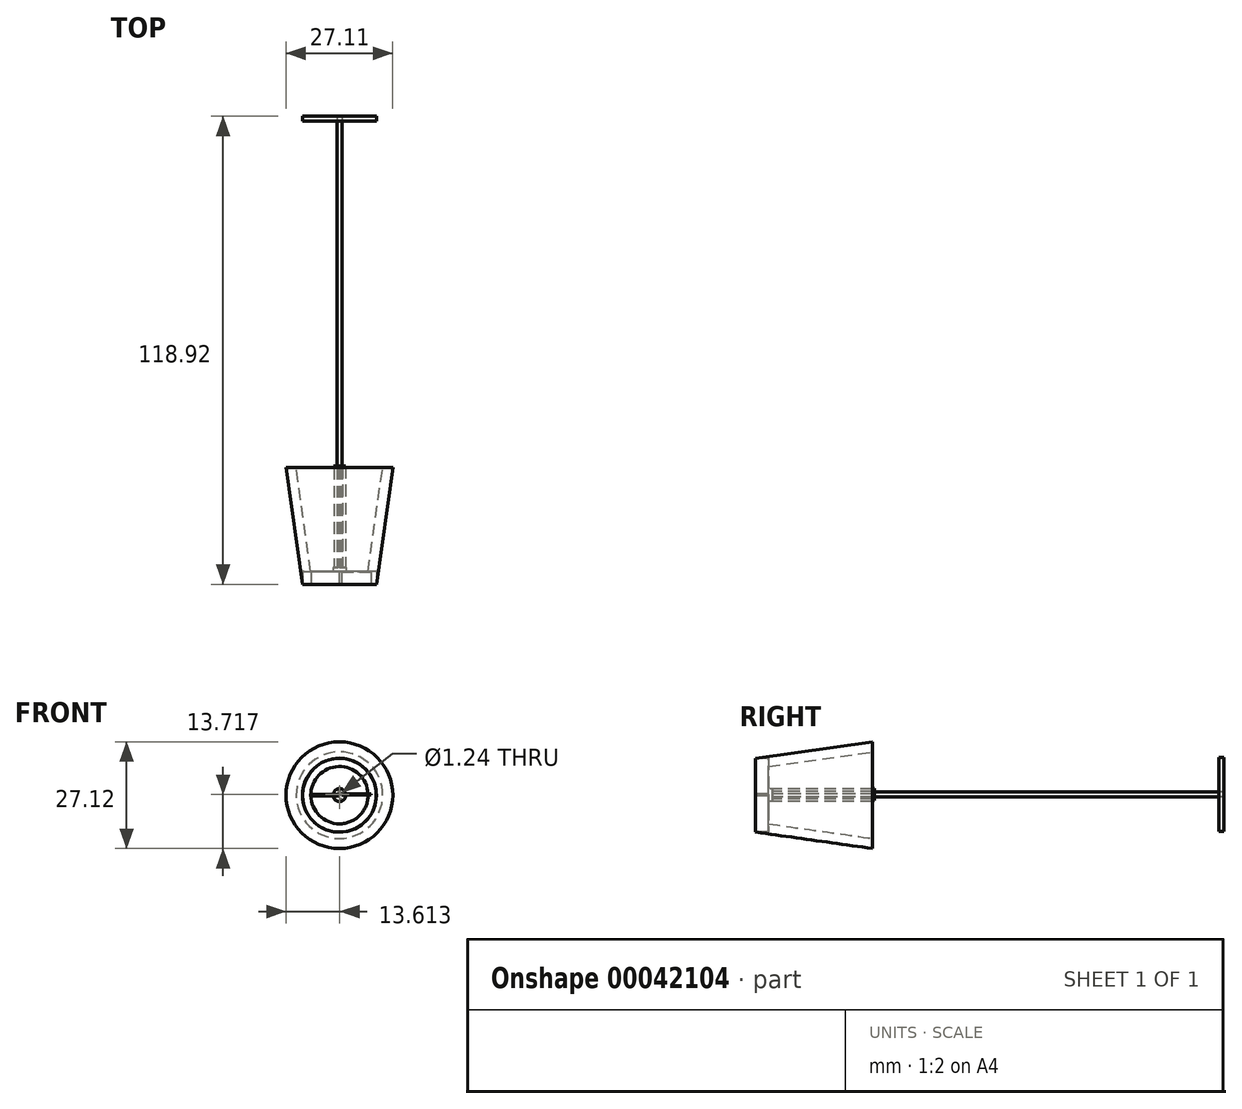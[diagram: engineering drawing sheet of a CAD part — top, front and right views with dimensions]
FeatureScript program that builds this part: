
annotation { "Feature Type Name" : "Feature", "Feature Type Description" : "" }
export const myFeature = defineFeature(function(context is Context, id is Id, definition is map)
    precondition{}
    {
        {
            var Q0;
            Q0=qCreatedBy(makeId("Front.planeOp"),FACE);
            var sketch = newSketch(context, id + "F0", { "sketchPlane" : qUnion([Q0])});
            skCircle(sketch, "E0", {"center": v(-47.5, -26.07) * mm, "radius": 13.56 * mm});
            skSolve(sketch);
        }
        {
            var Q0;
            Q0=makeQuery(id+"F0.imprint","IMPRINT",FACE,{"disambiguationData":[TD([[makeQuery(id+"F0.imprint","IMPRINT",EDGE,{"derivedFrom":sQuery(id+"F0.wireOp",EDGE,"E0")}),1.0]])]});
            extrude(context, id + "F1", {"entities" : qUnion([Q0]), "depth" : 29.72 * mm, "hasDraft" : true, "draftAngle" : 8 * degree, "draftPullDirection" : true});
        }
        {
            var Q0;
            Q0=makeQuery(id+"F1.opExtrude","CAP_FACE",FACE,{"disambiguationData":[OSD([sQuery(id+"F0.wireOp",EDGE,"E0")])],"isStart":true});
            shell(context, id + "F2", {"entities" : qUnion([Q0]), "thickness" : 2.54 * mm});
        }
        {
            var Q0;
            {var subQ0=sQuery(id+"F0.wireOp",EDGE,"E0");Q0=makeQuery(id+"F2.opShell","OFFSET_FACE",FACE,{"disambiguationData":[OSD([subQ0]),TDD([makeQuery(id+"F1.opExtrude","CAP_FACE",FACE,{"disambiguationData":[OSD([subQ0])],"isStart":false})])]});}
            var sketch = newSketch(context, id + "F3", { "sketchPlane" : qUnion([Q0])});
            skCircle(sketch, "E1", {"center": v(47.5, -26.07) * mm, "radius": 1.62 * mm});
            skSolve(sketch);
        }
        {
            var Q0;
            Q0=makeQuery(id+"F3.imprint","IMPRINT",FACE,{"disambiguationData":[TD([[makeQuery(id+"F3.imprint","IMPRINT",EDGE,{"derivedFrom":sQuery(id+"F3.wireOp",EDGE,"E1")}),1.0]])]});
            extrude(context, id + "F4", {"entities" : qUnion([Q0]), "operationType" : NewBodyOperationType.ADD, "depth" : 1.7 * mm});
        }
        {
            var Q0;
            Q0=makeQuery(id+"F4.opExtrude","CAP_FACE",FACE,{"disambiguationData":[OSD([sQuery(id+"F3.wireOp",EDGE,"E1")])],"isStart":false});
            var sketch = newSketch(context, id + "F5", { "sketchPlane" : qUnion([Q0])});
            skCircle(sketch, "E2", {"center": v(46.34, -26.1) * mm, "radius": 0.36 * mm});
            skCircle(sketch, "E3", {"center": v(47.5, -27.23) * mm, "radius": 0.4 * mm});
            skCircle(sketch, "E4", {"center": v(48.59, -26.1) * mm, "radius": 0.38 * mm});
            skCircle(sketch, "E5", {"center": v(47.36, -25.08) * mm, "radius": 0.42 * mm});
            skSolve(sketch);
        }
        {
            var Q0;
            Q0=makeQuery(id+"F5.imprint","IMPRINT",FACE,{"disambiguationData":[TD([[makeQuery(id+"F5.imprint","IMPRINT",EDGE,{"derivedFrom":sQuery(id+"F5.wireOp",EDGE,"E2")}),1.0]])]});
            extrude(context, id + "F6", {"entities" : qUnion([Q0]), "operationType" : NewBodyOperationType.ADD, "depth" : 25.7 * mm});
        }
        {
            var Q0;
            Q0=makeQuery(id+"F4.opExtrude","CAP_FACE",FACE,{"disambiguationData":[OSD([sQuery(id+"F3.wireOp",EDGE,"E1")])],"isStart":false});
            var sketch = newSketch(context, id + "F7", { "sketchPlane" : qUnion([Q0])});
            skCircle(sketch, "E6", {"center": v(48.47, -26.15) * mm, "radius": 0.36 * mm});
            skSolve(sketch);
        }
        {
            var Q0;
            Q0=makeQuery(id+"F7.imprint","IMPRINT",FACE,{"disambiguationData":[TD([[makeQuery(id+"F7.imprint","IMPRINT",EDGE,{"derivedFrom":sQuery(id+"F7.wireOp",EDGE,"E6")}),1.0]])]});
            extrude(context, id + "F8", {"entities" : qUnion([Q0]), "operationType" : NewBodyOperationType.ADD, "depth" : 25.4 * mm});
        }
        {
            var Q0;
            Q0=makeQuery(id+"F4.opExtrude","CAP_FACE",FACE,{"disambiguationData":[OSD([sQuery(id+"F3.wireOp",EDGE,"E1")])],"isStart":false});
            var sketch = newSketch(context, id + "F9", { "sketchPlane" : qUnion([Q0])});
            skCircle(sketch, "E7", {"center": v(47.58, -24.73) * mm, "radius": 0.33 * mm});
            skSolve(sketch);
        }
        {
            var Q0;
            {var subQ0=makeQuery(id+"F4.opExtrude","CAP_EDGE",EDGE,{"disambiguationData":[OSD([sQuery(id+"F3.wireOp",EDGE,"E1")])],"isStart":false});var subQ1=sQuery(id+"F9.wireOp",EDGE,"E7");var subQ3=makeQuery(id+"F9.imprint","INTERSECT",VERTEX,{"disambiguationData":[OD(0.0)],"derivedFrom":[subQ0,subQ1]});Q0=makeQuery(id+"F9.imprint","IMPRINT",FACE,{"disambiguationData":[TD([[makeQuery(id+"F9.imprint","IMPRINT",EDGE,{"disambiguationData":[TD([[subQ3,1.0]])],"derivedFrom":subQ1}),1.0]])]});}
            extrude(context, id + "F10", {"entities" : qUnion([Q0]), "operationType" : NewBodyOperationType.ADD, "depth" : 25.4 * mm});
        }
        {
            var Q0;
            Q0=makeQuery(id+"F4.opExtrude","CAP_FACE",FACE,{"disambiguationData":[OSD([sQuery(id+"F3.wireOp",EDGE,"E1")])],"isStart":false});
            var sketch = newSketch(context, id + "F11", { "sketchPlane" : qUnion([Q0])});
            skCircle(sketch, "E8", {"center": v(47.13, -27.35) * mm, "radius": 0.3 * mm});
            skSolve(sketch);
        }
        {
            var Q0;
            {var subQ0=makeQuery(id+"F4.opExtrude","CAP_EDGE",EDGE,{"disambiguationData":[OSD([sQuery(id+"F3.wireOp",EDGE,"E1")])],"isStart":false});var subQ1=sQuery(id+"F11.wireOp",EDGE,"E8");var subQ3=makeQuery(id+"F11.imprint","INTERSECT",VERTEX,{"disambiguationData":[OD(0.0)],"derivedFrom":[subQ0,subQ1]});Q0=makeQuery(id+"F11.imprint","IMPRINT",FACE,{"disambiguationData":[TD([[makeQuery(id+"F11.imprint","IMPRINT",EDGE,{"disambiguationData":[TD([[subQ3,-1.0]])],"derivedFrom":subQ1}),1.0]])]});}
            extrude(context, id + "F12", {"entities" : qUnion([Q0]), "operationType" : NewBodyOperationType.ADD, "depth" : 25.4 * mm});
        }
        {
            var Q0;
            Q0=makeQuery(id+"F10.opExtrude","CAP_FACE",FACE,{"disambiguationData":[OSD([sQuery(id+"F3.wireOp",EDGE,"E1"),sQuery(id+"F9.wireOp",EDGE,"E7")])],"isStart":false});
            var sketch = newSketch(context, id + "F13", { "sketchPlane" : qUnion([Q0])});
            skCircle(sketch, "E9", {"center": v(47.66, -25.95) * mm, "radius": 1.52 * mm});
            skPoint(sketch, "E9.first.point", {"position": v(47.42, -24.45) * mm});
            skPoint(sketch, "E9.second.point", {"position": v(47.07, -27.35) * mm});
            skPoint(sketch, "E9.third.point", {"position": v(47.42, -27.45) * mm});
            skSolve(sketch);
        }
        {
            var Q0;
            Q0=makeQuery(id+"F13.imprint","IMPRINT",FACE,{"disambiguationData":[TD([[makeQuery(id+"F13.imprint","IMPRINT",EDGE,{"derivedFrom":sQuery(id+"F13.wireOp",EDGE,"E9")}),1.0]])]});
            var sketch = newSketch(context, id + "F14", { "sketchPlane" : qUnion([Q0])});
            skCircle(sketch, "E10", {"center": v(47.44, -25.91) * mm, "radius": 1.54 * mm});
            skSolve(sketch);
        }
        {
            var Q0;
            Q0 = qSketchRegion(id + "F14", true);
            extrude(context, id + "F15", {"entities" : qUnion([Q0]), "depth" : 0.5 * mm});
        }
        {
            var Q0;
            Q0=makeQuery(id+"F15.opExtrude","CAP_FACE",FACE,{"disambiguationData":[OSD([sQuery(id+"F14.wireOp",EDGE,"E10")])],"isStart":false});
            var sketch = newSketch(context, id + "F16", { "sketchPlane" : qUnion([Q0])});
            skCircle(sketch, "E11", {"center": v(47.44, -25.91) * mm, "radius": 0.62 * mm});
            skSolve(sketch);
        }
        {
            var Q0;
            Q0=makeQuery(id+"F16.imprint","IMPRINT",FACE,{"disambiguationData":[TD([[makeQuery(id+"F16.imprint","IMPRINT",EDGE,{"derivedFrom":sQuery(id+"F16.wireOp",EDGE,"E11")}),1.0]])]});
            extrude(context, id + "F17", {"entities" : qUnion([Q0]), "operationType" : NewBodyOperationType.ADD, "depth" : 87.55 * mm});
        }
        {
            var Q0;
            Q0=makeQuery(id+"F17.opExtrude","CAP_FACE",FACE,{"disambiguationData":[OSD([sQuery(id+"F16.wireOp",EDGE,"E11")])],"isStart":false});
            var sketch = newSketch(context, id + "F18", { "sketchPlane" : qUnion([Q0])});
            skCircle(sketch, "E12", {"center": v(47.44, -25.91) * mm, "radius": 9.4 * mm});
            skSolve(sketch);
        }
        {
            var Q0;
            Q0=makeQuery(id+"F18.imprint","IMPRINT",FACE,{"disambiguationData":[TD([[makeQuery(id+"F18.imprint","IMPRINT",EDGE,{"derivedFrom":sQuery(id+"F18.wireOp",EDGE,"E12")}),1.0]])]});
            extrude(context, id + "F19", {"entities" : qUnion([Q0]), "depth" : 1.24 * mm});
        }
        {
            var Q0;
            Q0=makeQuery(id+"F1.opExtrude","CAP_FACE",FACE,{"disambiguationData":[OSD([sQuery(id+"F0.wireOp",EDGE,"E0")])],"isStart":false});
            var sketch = newSketch(context, id + "F20", { "sketchPlane" : qUnion([Q0])});
            skCircle(sketch, "E13", {"center": v(-47.5, -26.07) * mm, "radius": 10.69 * mm});
            skSolve(sketch);
        }
        {
            var Q0;
            Q0=makeQuery(id+"F20.imprint","IMPRINT",FACE,{"disambiguationData":[TD([[makeQuery(id+"F20.imprint","IMPRINT",EDGE,{"derivedFrom":makeQuery(id+"F1.opExtrude","CAP_EDGE",EDGE,{"disambiguationData":[OSD([sQuery(id+"F0.wireOp",EDGE,"E0")])],"isStart":false})}),1.0]])]});
            var sketch = newSketch(context, id + "F21", { "sketchPlane" : qUnion([Q0])});
            skCircle(sketch, "E14", {"center": v(-47.52, -26) * mm, "radius": 9.5 * mm});
            skSolve(sketch);
        }
        {
            var Q0;
            Q0=makeQuery(id+"F20.imprint","IMPRINT",FACE,{"disambiguationData":[TD([[makeQuery(id+"F20.imprint","IMPRINT",EDGE,{"derivedFrom":makeQuery(id+"F1.opExtrude","CAP_EDGE",EDGE,{"disambiguationData":[OSD([sQuery(id+"F0.wireOp",EDGE,"E0")])],"isStart":false})}),1.0]])]});
            var sketch = newSketch(context, id + "F22", { "sketchPlane" : qUnion([Q0])});
            skCircle(sketch, "E15", {"center": v(-47.43, -26.05) * mm, "radius": 9.45 * mm});
            skSolve(sketch);
        }
        {
            var Q0;
            {var subQ0=makeQuery(id+"F20.imprint","IMPRINT",EDGE,{"derivedFrom":makeQuery(id+"F1.opExtrude","CAP_EDGE",EDGE,{"disambiguationData":[OSD([sQuery(id+"F0.wireOp",EDGE,"E0")])],"isStart":false})});var subQ1=sQuery(id+"F22.wireOp",EDGE,"E15");var subQ3=makeQuery(id+"F22.imprint","INTERSECT",VERTEX,{"disambiguationData":[OD(0.0)],"derivedFrom":[subQ0,subQ1]});Q0=makeQuery(id+"F22.imprint","IMPRINT",FACE,{"disambiguationData":[TD([[makeQuery(id+"F22.imprint","IMPRINT",EDGE,{"disambiguationData":[TD([[subQ3,-1.0]])],"derivedFrom":subQ1}),1.0]])]});}
            extrude(context, id + "F23", {"entities" : qUnion([Q0]), "operationType" : NewBodyOperationType.REMOVE, "oppositeDirection" : true, "depth" : 3.27 * mm});
        }
        {
            var Q0;
            Q0=makeQuery(id+"F21.imprint","IMPRINT",FACE,{"disambiguationData":[TD([[makeQuery(id+"F21.imprint","IMPRINT",EDGE,{"derivedFrom":makeQuery(id+"F20.imprint","IMPRINT",EDGE,{"derivedFrom":makeQuery(id+"F1.opExtrude","CAP_EDGE",EDGE,{"disambiguationData":[OSD([sQuery(id+"F0.wireOp",EDGE,"E0")])],"isStart":false})})}),1.0]])]});
            var sketch = newSketch(context, id + "F24", { "sketchPlane" : qUnion([Q0])});
            skLineSegment(sketch, "E16.bottom", {"start": v(-54.67, -25.9) * mm, "end": v(-47.59, -25.9) * mm});
            skLineSegment(sketch, "E16.top", {"start": v(-54.67, -26.2) * mm, "end": v(-47.59, -26.2) * mm});
            skLineSegment(sketch, "E16.left", {"start": v(-54.67, -25.9) * mm, "end": v(-54.67, -26.2) * mm});
            skLineSegment(sketch, "E16.right", {"start": v(-47.59, -25.9) * mm, "end": v(-47.59, -26.2) * mm});
            skSolve(sketch);
        }
        {
            var Q0;
            Q0 = qSketchRegion(id + "F24", true);
            extrude(context, id + "F25", {"entities" : qUnion([Q0]), "oppositeDirection" : true, "depth" : 3.23 * mm});
        }
        {
            var Q0;
            Q0=makeQuery(id+"F21.imprint","IMPRINT",FACE,{"disambiguationData":[TD([[makeQuery(id+"F21.imprint","IMPRINT",EDGE,{"derivedFrom":makeQuery(id+"F20.imprint","IMPRINT",EDGE,{"derivedFrom":makeQuery(id+"F1.opExtrude","CAP_EDGE",EDGE,{"disambiguationData":[OSD([sQuery(id+"F0.wireOp",EDGE,"E0")])],"isStart":false})})}),1.0]])]});
            var sketch = newSketch(context, id + "F26", { "sketchPlane" : qUnion([Q0])});
            skLineSegment(sketch, "E17.bottom", {"start": v(-46.92, -25.75) * mm, "end": v(-39.42, -25.75) * mm});
            skLineSegment(sketch, "E17.top", {"start": v(-46.92, -26.04) * mm, "end": v(-39.42, -26.04) * mm});
            skLineSegment(sketch, "E17.left", {"start": v(-46.92, -25.75) * mm, "end": v(-46.92, -26.04) * mm});
            skLineSegment(sketch, "E17.right", {"start": v(-39.42, -25.75) * mm, "end": v(-39.42, -26.04) * mm});
            skSolve(sketch);
        }
        {
            var Q0;
            Q0 = qSketchRegion(id + "F26", true);
            extrude(context, id + "F27", {"entities" : qUnion([Q0]), "oppositeDirection" : true, "depth" : 3.16 * mm});
        }
    });
